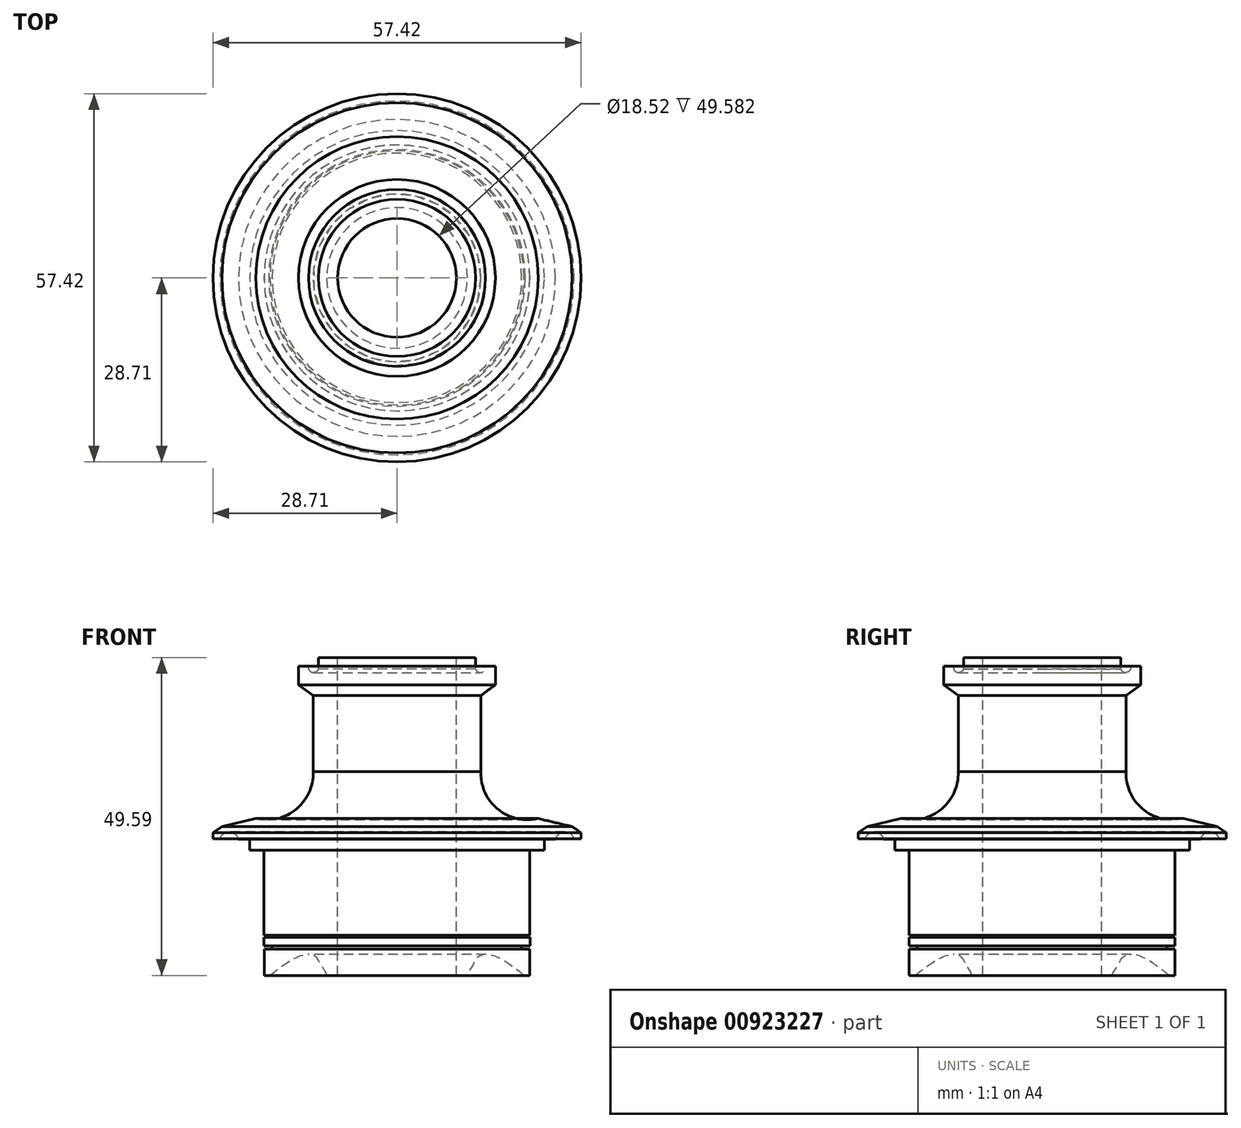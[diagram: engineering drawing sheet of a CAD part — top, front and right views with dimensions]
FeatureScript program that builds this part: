
annotation { "Feature Type Name" : "Feature", "Feature Type Description" : "" }
export const myFeature = defineFeature(function(context is Context, id is Id, definition is map)
    precondition{}
    {
        {
            var Q0;
            Q0=qCreatedBy(makeId("Front.planeOp"),FACE);
            var sketch = newSketch(context, id + "F0", { "sketchPlane" : qUnion([Q0])});
            skLineSegment(sketch, "E0", {"start": v(9.26, 26.37) * mm, "end": v(9.26, -23.2) * mm});
            skLineSegment(sketch, "E1", {"start": v(9.26, -23.2) * mm, "end": v(10.96, -23.2) * mm});
            skLineSegment(sketch, "E2", {"start": v(9.26, 26.37) * mm, "end": v(12.26, 26.37) * mm});
            skLineSegment(sketch, "E3", {"start": v(13.8, 25) * mm, "end": v(15.35, 25) * mm});
            skLineSegment(sketch, "E4", {"start": v(15.35, 25) * mm, "end": v(15.35, 22.13) * mm});
            skLineSegment(sketch, "E5", {"start": v(15.35, 22.13) * mm, "end": v(13.08, 20.42) * mm});
            skLineSegment(sketch, "E6", {"start": v(13.08, 20.42) * mm, "end": v(13.08, 8.55) * mm});
            skLineSegment(sketch, "E7", {"start": v(22.03, 1.24) * mm, "end": v(27.32, 0) * mm});
            skLineSegment(sketch, "E8", {"start": v(27.32, 0) * mm, "end": v(28.71, -0.97) * mm});
            skLineSegment(sketch, "E9", {"start": v(28.71, -0.97) * mm, "end": v(28.71, -1.92) * mm});
            skLineSegment(sketch, "E10", {"start": v(28.71, -1.92) * mm, "end": v(27.62, -1.92) * mm});
            skLineSegment(sketch, "E11", {"start": v(24.72, -2) * mm, "end": v(22.98, -2) * mm});
            skLineSegment(sketch, "E12", {"start": v(22.98, -2) * mm, "end": v(22.98, -3.68) * mm});
            skLineSegment(sketch, "E13", {"start": v(22.98, -3.68) * mm, "end": v(20.73, -3.68) * mm});
            skLineSegment(sketch, "E14", {"start": v(20.73, -3.68) * mm, "end": v(20.73, -16.93) * mm});
            skLineSegment(sketch, "E15", {"start": v(20.73, -16.93) * mm, "end": v(20.02, -16.93) * mm});
            skLineSegment(sketch, "E16", {"start": v(20.02, -17.23) * mm, "end": v(20.74, -17.24) * mm});
            skLineSegment(sketch, "E17", {"start": v(20.74, -17.24) * mm, "end": v(20.74, -18.58) * mm});
            skLineSegment(sketch, "E18", {"start": v(20.74, -18.58) * mm, "end": v(19.47, -18.58) * mm});
            skLineSegment(sketch, "E19", {"start": v(19.47, -18.58) * mm, "end": v(19.47, -19.12) * mm});
            skLineSegment(sketch, "E20", {"start": v(19.47, -19.12) * mm, "end": v(20.73, -19.12) * mm});
            skLineSegment(sketch, "E21", {"start": v(20.73, -19.12) * mm, "end": v(20.73, -23.22) * mm});
            skLineSegment(sketch, "E22", {"start": v(20.73, -23.22) * mm, "end": v(19.82, -23.22) * mm});
            skArc(sketch, "E23", {"start": v(13.8, 25) * mm, "mid": v(13.23, 24.05) * mm, "end": v(12.26, 24.6) * mm});
            skArc(sketch, "E24", {"start": v(13.08, 8.55) * mm, "mid": v(15.75, 2.68) * mm, "end": v(22.03, 1.24) * mm});
            skLineSegment(sketch, "E25", {"start": v(12.26, 24.6) * mm, "end": v(12.26, 26.37) * mm});
            skArc(sketch, "E26", {"start": v(27.62, -1.92) * mm, "mid": v(26.14, -0.85) * mm, "end": v(24.72, -2) * mm});
            skLineSegment(sketch, "E27", {"start": v(20.02, -17.23) * mm, "end": v(20.02, -16.93) * mm});
            skFitSpline(sketch, "E28", {"points": [v(19.82, -23.22) * mm, v(14.86, -20.1) * mm, v(12.6, -20.35) * mm, v(11.83, -21.62) * mm, v(10.96, -23.2) * mm], "startDerivative": vector(-13.86, 10.85) * mm, "endDerivative": vector(-1.18, -8.12) * mm});
            skLineSegment(sketch, "E29", {"start": v(0, 27.82) * mm, "end": v(0, -32.43) * mm});
            skSolve(sketch);
        }
        {
            var Q0;
            Q0 = qSketchRegion(id + "F0", true);
            var Q1;
            Q1=sQuery(id+"F0.wireOp",EDGE,"E29");
            revolve(context, id + "F1", {"surfaceOperationType" : NewSurfaceOperationType.NEW, "entities" : qUnion([Q0]), "axis" : qUnion([Q1]), "revolveType" : RevolveType.FULL});
        }
    });
